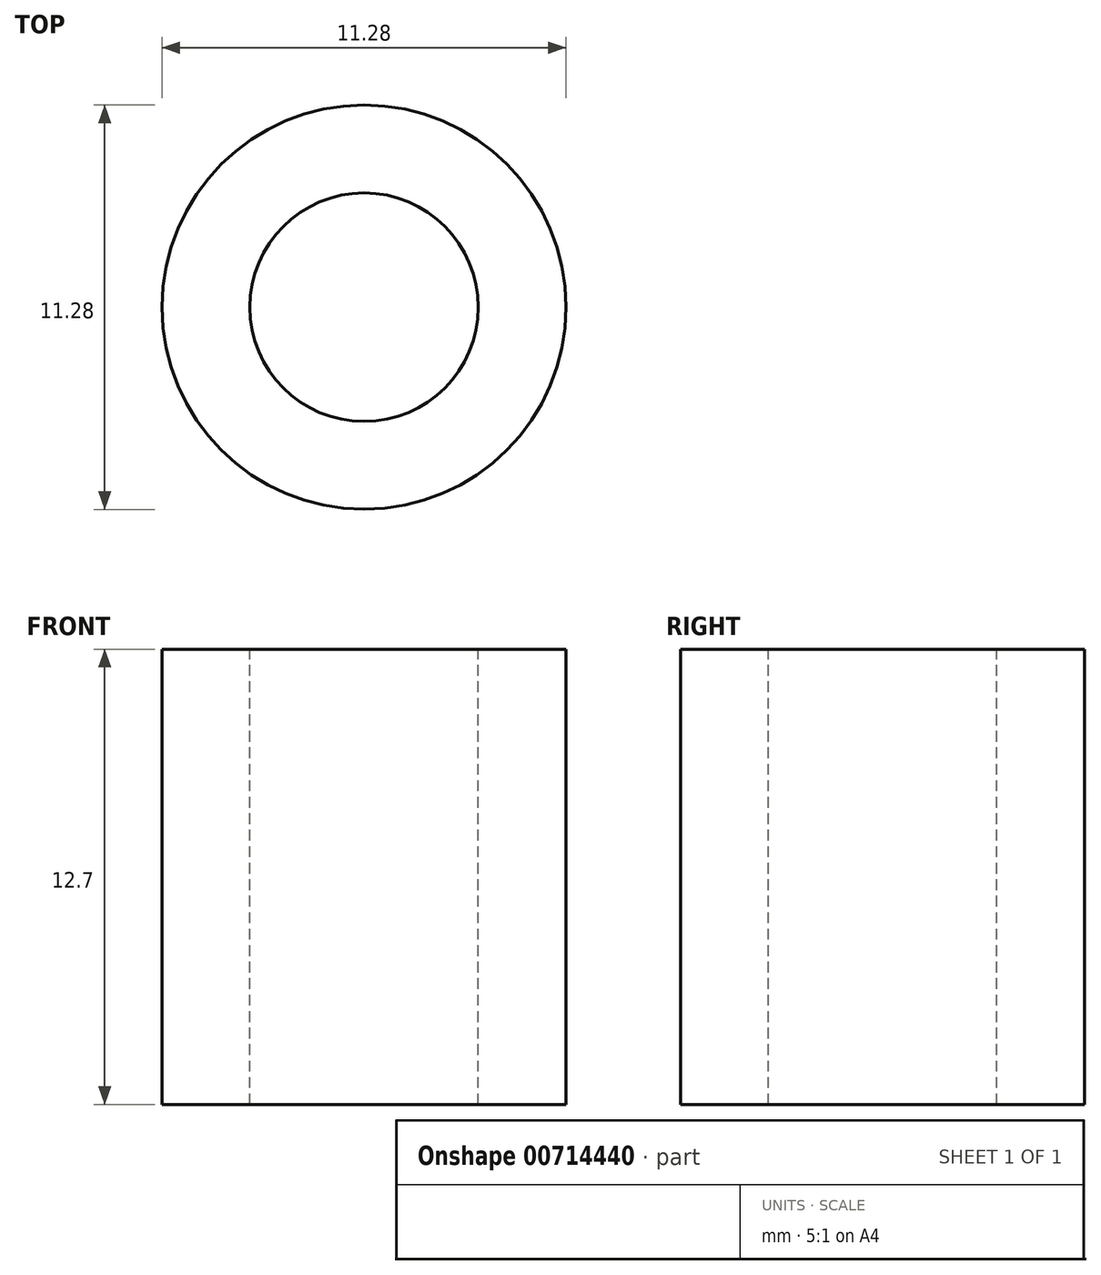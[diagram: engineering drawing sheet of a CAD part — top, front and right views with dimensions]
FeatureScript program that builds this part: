
annotation { "Feature Type Name" : "Feature", "Feature Type Description" : "" }
export const myFeature = defineFeature(function(context is Context, id is Id, definition is map)
    precondition{}
    {
        {
            var Q0;
            Q0=qCreatedBy(makeId("Top.planeOp"),FACE);
            var sketch = newSketch(context, id + "F0", { "sketchPlane" : qUnion([Q0])});
            skCircle(sketch, "E0", {"center": v(0, 0) * mm, "radius": 5.64 * mm});
            skSolve(sketch);
        }
        {
            var Q0;
            Q0=makeQuery(id+"F0.imprint","IMPRINT",FACE,{"disambiguationData":[TD([[makeQuery(id+"F0.imprint","IMPRINT",EDGE,{"derivedFrom":sQuery(id+"F0.wireOp",EDGE,"E0")}),1.0]])]});
            extrude(context, id + "F1", {"entities" : qUnion([Q0]), "oppositeDirection" : true, "depth" : 12.7 * mm});
        }
        {
            var Q0;
            Q0=makeQuery(id+"F1.opExtrude","CAP_FACE",FACE,{"disambiguationData":[OSD([sQuery(id+"F0.wireOp",EDGE,"E0")])],"isStart":true});
            var sketch = newSketch(context, id + "F2", { "sketchPlane" : qUnion([Q0])});
            skCircle(sketch, "E1", {"center": v(0, 0) * mm, "radius": 3.19 * mm});
            skSolve(sketch);
        }
        {
            var Q0;
            Q0=qSketchRegion(id+"F2",true);
            extrude(context, id + "F3", {"entities" : qUnion([Q0]), "operationType" : NewBodyOperationType.REMOVE, "endBound" : BoundingType.THROUGH_ALL, "oppositeDirection" : true, "depth" : 25.4 * mm});
        }
    });
